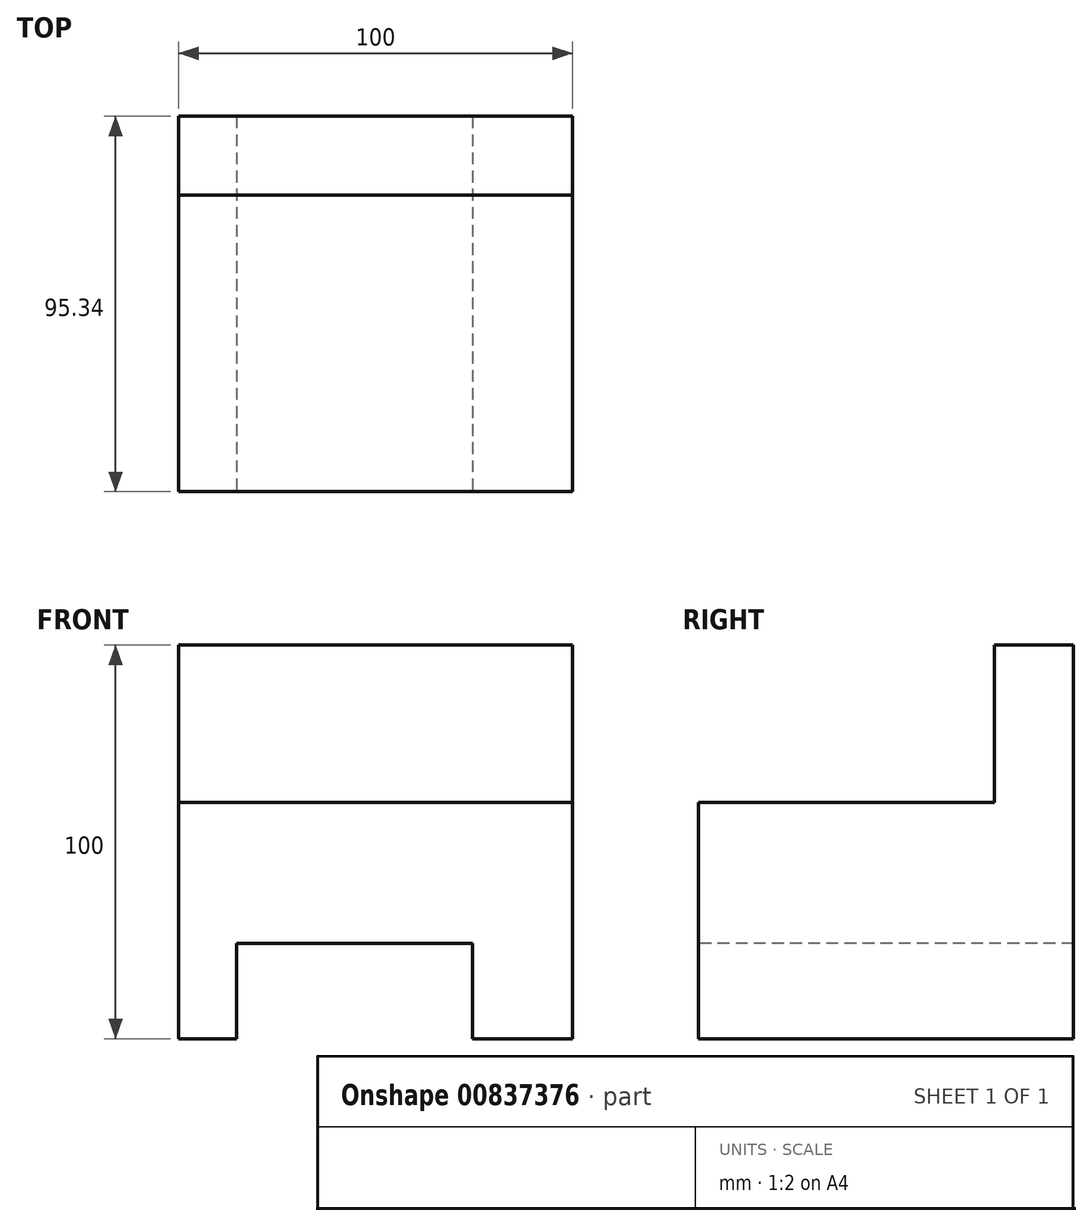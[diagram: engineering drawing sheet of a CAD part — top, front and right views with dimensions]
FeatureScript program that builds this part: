
annotation { "Feature Type Name" : "Feature", "Feature Type Description" : "" }
export const myFeature = defineFeature(function(context is Context, id is Id, definition is map)
    precondition{}
    {
        {
            var Q0;
            Q0=qCreatedBy(makeId("Top.planeOp"),FACE);
            var sketch = newSketch(context, id + "F0", { "sketchPlane" : qUnion([Q0])});
            skLineSegment(sketch, "E0.bottom", {"start": v(50, -47.67) * mm, "end": v(-50, -47.67) * mm});
            skLineSegment(sketch, "E0.top", {"start": v(50, 47.67) * mm, "end": v(-50, 47.67) * mm});
            skLineSegment(sketch, "E0.left", {"start": v(50, -47.67) * mm, "end": v(50, 47.67) * mm});
            skLineSegment(sketch, "E0.right", {"start": v(-50, -47.67) * mm, "end": v(-50, 47.67) * mm});
            skPoint(sketch, "E0.middle", {"position": v(0, 0) * mm});
            skSolve(sketch);
        }
        {
            var Q0;
            Q0 = qSketchRegion(id + "F0", true);
            extrude(context, id + "F1", {"entities" : qUnion([Q0]), "depth" : 100 * mm, "offsetDistance" : 25 * mm});
        }
        {
            var Q0;
            Q0=makeQuery(id+"F1.opExtrude","CAP_FACE",FACE,{"disambiguationData":[OSD([sQuery(id+"F0.wireOp",EDGE,"E0.bottom"),sQuery(id+"F0.wireOp",EDGE,"E0.top"),sQuery(id+"F0.wireOp",EDGE,"E0.left"),sQuery(id+"F0.wireOp",EDGE,"E0.right")])],"isStart":false});
            var sketch = newSketch(context, id + "F2", { "sketchPlane" : qUnion([Q0])});
            skLineSegment(sketch, "E1.bottom", {"start": v(50, -47.67) * mm, "end": v(-50, -47.67) * mm});
            skLineSegment(sketch, "E1.top", {"start": v(50, 27.62) * mm, "end": v(-50, 27.62) * mm});
            skLineSegment(sketch, "E1.left", {"start": v(50, -47.67) * mm, "end": v(50, 27.62) * mm});
            skLineSegment(sketch, "E1.right", {"start": v(-50, -47.67) * mm, "end": v(-50, 27.62) * mm});
            skSolve(sketch);
        }
        {
            var Q0;
            Q0 = qSketchRegion(id + "F2", true);
            extrude(context, id + "F3", {"entities" : qUnion([Q0]), "operationType" : NewBodyOperationType.REMOVE, "oppositeDirection" : true, "depth" : 40 * mm, "offsetDistance" : 25 * mm});
        }
        {
            var Q0;
            Q0=makeQuery(id+"F1.opExtrude","SWEPT_FACE",FACE,{"disambiguationData":[OSD([sQuery(id+"F0.wireOp",EDGE,"E0.bottom")])]});
            var sketch = newSketch(context, id + "F4", { "sketchPlane" : qUnion([Q0])});
            skLineSegment(sketch, "E2.bottom", {"start": v(-35.32, 24.18) * mm, "end": v(24.68, 24.18) * mm});
            skLineSegment(sketch, "E2.top", {"start": v(-35.32, -15.82) * mm, "end": v(24.68, -15.82) * mm});
            skLineSegment(sketch, "E2.left", {"start": v(-35.32, 24.18) * mm, "end": v(-35.32, -15.82) * mm});
            skLineSegment(sketch, "E2.right", {"start": v(24.68, 24.18) * mm, "end": v(24.68, -15.82) * mm});
            skSolve(sketch);
        }
        {
            var Q0;
            {var subQ0=sQuery(id+"F4.wireOp",EDGE,"E2.top");Q0=makeQuery(id+"F4.imprint","IMPRINT",FACE,{"disambiguationData":[TD([[makeQuery(id+"F4.imprint","IMPRINT",EDGE,{"derivedFrom":subQ0}),1.0]])]});}
            var Q1;
            {var subQ0=sQuery(id+"F4.wireOp",EDGE,"E2.bottom");Q1=makeQuery(id+"F4.imprint","IMPRINT",FACE,{"disambiguationData":[TD([[makeQuery(id+"F4.imprint","IMPRINT",EDGE,{"derivedFrom":subQ0}),-1.0]])]});}
            extrude(context, id + "F5", {"entities" : qUnion([Q0, Q1]), "operationType" : NewBodyOperationType.REMOVE, "endBound" : BoundingType.THROUGH_ALL, "oppositeDirection" : true, "depth" : 25 * mm, "offsetDistance" : 25 * mm});
        }
    });
